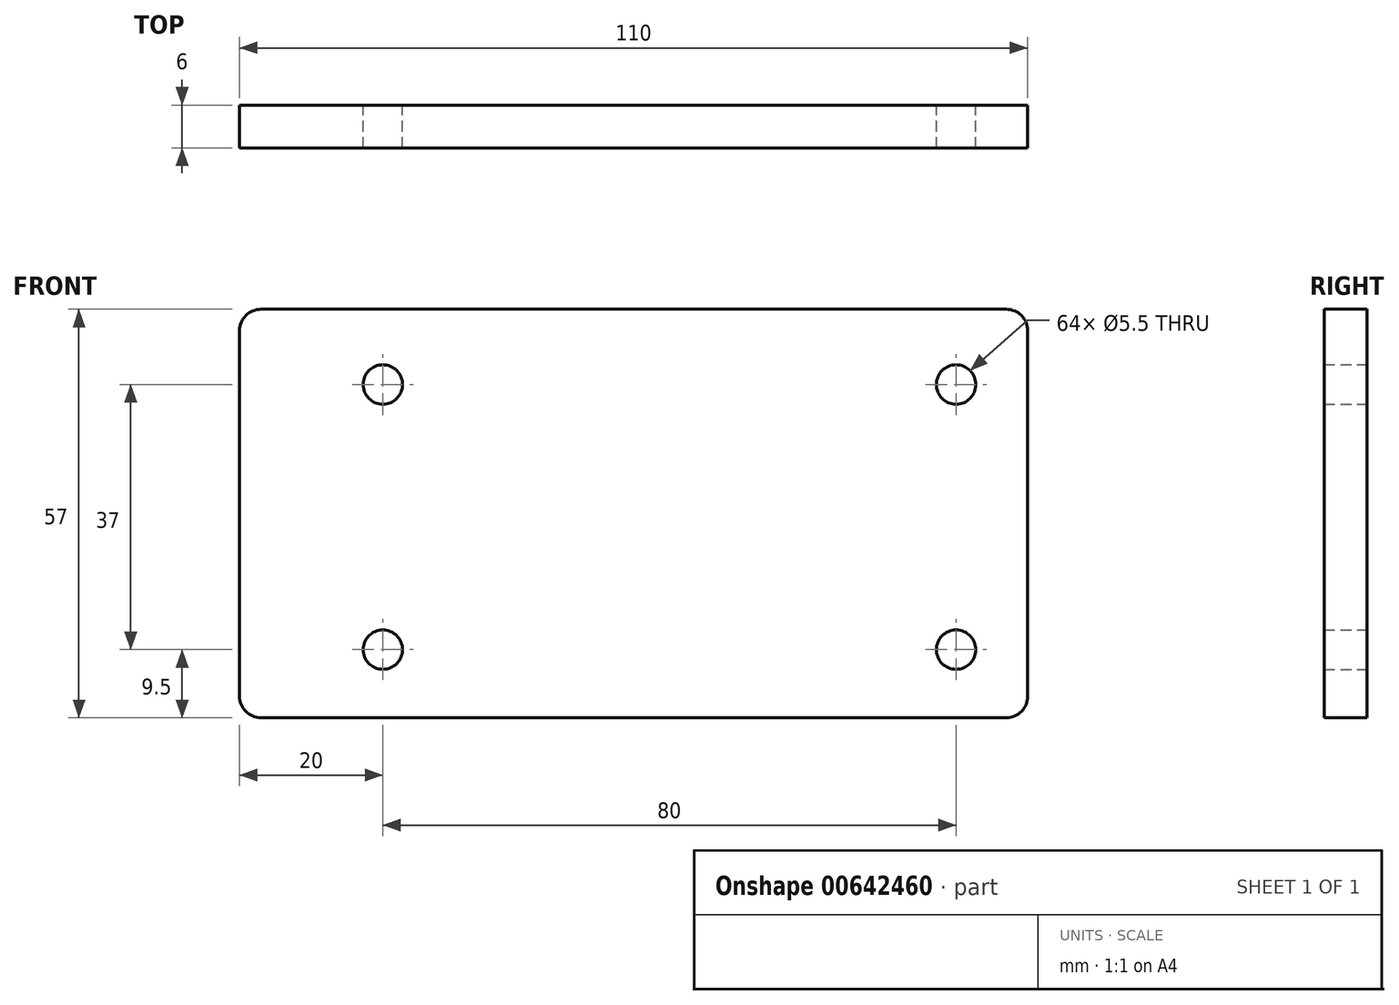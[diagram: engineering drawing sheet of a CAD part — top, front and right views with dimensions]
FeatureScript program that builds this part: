
annotation { "Feature Type Name" : "Feature", "Feature Type Description" : "" }
export const myFeature = defineFeature(function(context is Context, id is Id, definition is map)
    precondition{}
    {
        {
            var Q0;
            Q0=qCreatedBy(makeId("Front.planeOp"),FACE);
            var sketch = newSketch(context, id + "F0", { "sketchPlane" : qUnion([Q0])});
            skLineSegment(sketch, "E0.bottom", {"start": v(3, 0) * mm, "end": v(107, 0) * mm});
            skLineSegment(sketch, "E0.top", {"start": v(3, 57) * mm, "end": v(107, 57) * mm});
            skLineSegment(sketch, "E0.left", {"start": v(0, 3) * mm, "end": v(0, 54) * mm});
            skLineSegment(sketch, "E0.right", {"start": v(110, 3) * mm, "end": v(110, 54) * mm});
            skPoint(sketch, "E1.visualSharp", {"position": v(0, 57) * mm});
            skArc(sketch, "E1.filletArc", {"start": v(3, 57) * mm, "mid": v(0.88, 56.12) * mm, "end": v(0, 54) * mm});
            skPoint(sketch, "E2.visualSharp", {"position": v(0, 0) * mm});
            skArc(sketch, "E2.filletArc", {"start": v(0, 3) * mm, "mid": v(0.88, 0.88) * mm, "end": v(3, 0) * mm});
            skPoint(sketch, "E3.visualSharp", {"position": v(110, 0) * mm});
            skArc(sketch, "E3.filletArc", {"start": v(107, 0) * mm, "mid": v(109.12, 0.88) * mm, "end": v(110, 3) * mm});
            skPoint(sketch, "E4.visualSharp", {"position": v(110, 57) * mm});
            skArc(sketch, "E4.filletArc", {"start": v(110, 54) * mm, "mid": v(109.12, 56.12) * mm, "end": v(107, 57) * mm});
            skCircle(sketch, "E5", {"center": v(20, 46.5) * mm, "radius": 2.75 * mm});
            skCircle(sketch, "E6.0.1.0", {"center": v(20, 9.5) * mm, "radius": 2.75 * mm});
            skCircle(sketch, "E6.1.0.0", {"center": v(100, 46.5) * mm, "radius": 2.75 * mm});
            skCircle(sketch, "E6.1.1.0", {"center": v(100, 9.5) * mm, "radius": 2.75 * mm});
            skLineSegment(sketch, "E6.direction1", {"start": v(20, 46.5) * mm, "end": v(100, 46.5) * mm, "construction": true});
            skLineSegment(sketch, "E6.direction2", {"start": v(20, 46.5) * mm, "end": v(20, 9.5) * mm, "construction": true});
            skSolve(sketch);
        }
        {
            var Q0;
            Q0 = qSketchRegion(id + "F0", true);
            extrude(context, id + "F1", {"entities" : qUnion([Q0]), "depth" : 6 * mm, "offsetDistance" : 25 * mm});
        }
    });
